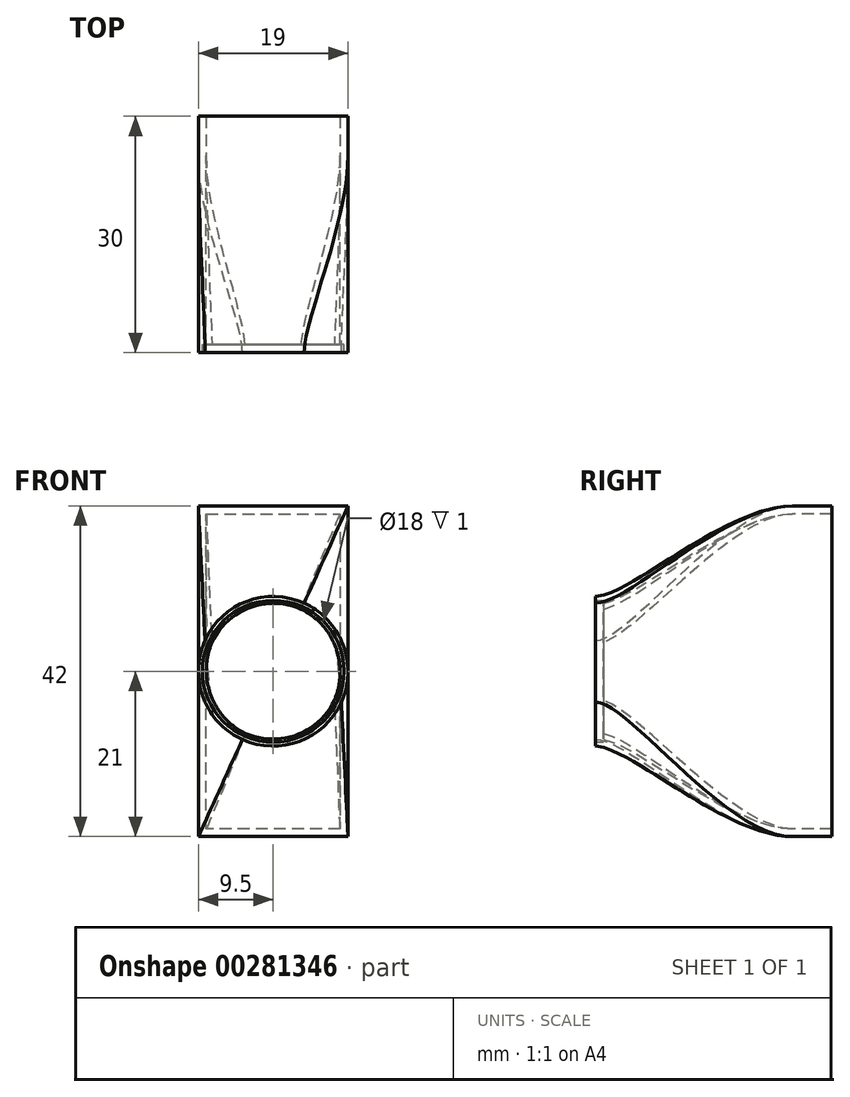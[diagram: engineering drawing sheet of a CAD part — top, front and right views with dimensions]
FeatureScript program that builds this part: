
annotation { "Feature Type Name" : "Feature", "Feature Type Description" : "" }
export const myFeature = defineFeature(function(context is Context, id is Id, definition is map)
    precondition{}
    {
        {
            var Q0;
            Q0=qCreatedBy(makeId("Front.planeOp"),FACE);
            var sketch = newSketch(context, id + "F0", { "sketchPlane" : qUnion([Q0])});
            skCircle(sketch, "E0", {"center": v(0, 0) * mm, "radius": 9.5 * mm});
            skSolve(sketch);
        }
        {
            var Q0;
            Q0=qCreatedBy(makeId("Front.planeOp"),FACE);
            cPlane(context, id + "F1", {"entities" : qUnion([Q0]), "cplaneType" : CPlaneType.OFFSET, "offset" : 25 * mm, "oppositeDirection" : true, "width" : 150 * mm, "height" : 150 * mm});
        }
        {
            var Q0;
            Q0=qCreatedBy(id+"F1.planeOp",FACE);
            var sketch = newSketch(context, id + "F2", { "sketchPlane" : qUnion([Q0])});
            skLineSegment(sketch, "E1.bottom", {"start": v(9.5, 21) * mm, "end": v(-9.5, 21) * mm});
            skLineSegment(sketch, "E1.top", {"start": v(9.5, -21) * mm, "end": v(-9.5, -21) * mm});
            skLineSegment(sketch, "E1.left", {"start": v(9.5, 21) * mm, "end": v(9.5, -21) * mm});
            skLineSegment(sketch, "E1.right", {"start": v(-9.5, 21) * mm, "end": v(-9.5, -21) * mm});
            skPoint(sketch, "E1.middle", {"position": v(0, 0) * mm});
            skSolve(sketch);
        }
        {
            var Q0;
            Q0=qCreatedBy(makeId("Front.planeOp"),FACE);
            cPlane(context, id + "F3", {"entities" : qUnion([Q0]), "cplaneType" : CPlaneType.OFFSET, "offset" : 5 * mm, "oppositeDirection" : true, "width" : 150 * mm, "height" : 150 * mm});
        }
        {
            var Q0;
            Q0=qCreatedBy(id+"F3.planeOp",FACE);
            var sketch = newSketch(context, id + "F4", { "sketchPlane" : qUnion([Q0])});
            skCircle(sketch, "E2", {"center": v(0, 0) * mm, "radius": 9 * mm});
            skSolve(sketch);
        }
        {
            var Q0;
            Q0=makeQuery(id+"F0.imprint","IMPRINT",FACE,{"disambiguationData":[TD([[makeQuery(id+"F0.imprint","IMPRINT",EDGE,{"derivedFrom":sQuery(id+"F0.wireOp",EDGE,"E0")}),1.0]])]});
            var Q1;
            Q1=makeQuery(id+"F2.imprint","IMPRINT",FACE,{"disambiguationData":[TD([[makeQuery(id+"F2.imprint","IMPRINT",EDGE,{"derivedFrom":sQuery(id+"F2.wireOp",EDGE,"E1.bottom")}),1.0]])]});
            loft(context, id + "F5", {"startCondition" : LoftEndDerivativeType.NORMAL_TO_PROFILE, "startMagnitude" : 0.5, "endCondition" : LoftEndDerivativeType.NORMAL_TO_PROFILE, "endMagnitude" : 1, "sheetProfilesArray" : [{ "sheetProfileEntities" : qUnion([Q0]) }, { "sheetProfileEntities" : qUnion([Q1]) }]});
        }
        {
            var Q0;
            Q0=makeQuery(id+"F5.opLoft","CAP_FACE",FACE,{"disambiguationData":[OSD([makeQuery(id+"F2.imprint","IMPRINT",FACE,{"disambiguationData":[TD([[makeQuery(id+"F2.imprint","IMPRINT",EDGE,{"derivedFrom":sQuery(id+"F2.wireOp",EDGE,"E1.bottom")}),1.0]])]})])],"isStart":true});
            extrude(context, id + "F6", {"entities" : qUnion([Q0]), "operationType" : NewBodyOperationType.ADD, "depth" : 5 * mm});
        }
        {
            var Q0;
            Q0=makeQuery(id+"F6.opExtrude","CAP_FACE",FACE,{"disambiguationData":[OSD([makeQuery(id+"F2.imprint","IMPRINT",FACE,{"disambiguationData":[TD([[makeQuery(id+"F2.imprint","IMPRINT",EDGE,{"derivedFrom":sQuery(id+"F2.wireOp",EDGE,"E1.bottom")}),1.0]])]})])],"isStart":false});
            shell(context, id + "F7", {"entities" : qUnion([Q0]), "thickness" : 1 * mm});
        }
        {
            var Q0;
            Q0=makeQuery(id+"F7.opShell","OFFSET_FACE",FACE,{"disambiguationData":[OSD([makeQuery(id+"F0.imprint","IMPRINT",FACE,{"disambiguationData":[TD([[makeQuery(id+"F0.imprint","IMPRINT",EDGE,{"derivedFrom":sQuery(id+"F0.wireOp",EDGE,"E0")}),1.0]])]})])]});
            var sketch = newSketch(context, id + "F8", { "sketchPlane" : qUnion([Q0])});
            skCircle(sketch, "E3", {"center": v(0, 0) * mm, "radius": 9 * mm});
            skSolve(sketch);
        }
        {
            var Q0;
            Q0 = qSketchRegion(id + "F8", true);
            extrude(context, id + "F9", {"entities" : qUnion([Q0]), "operationType" : NewBodyOperationType.REMOVE, "oppositeDirection" : true, "depth" : 25 * mm});
        }
    });
